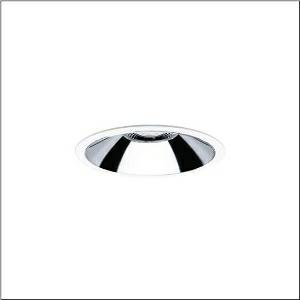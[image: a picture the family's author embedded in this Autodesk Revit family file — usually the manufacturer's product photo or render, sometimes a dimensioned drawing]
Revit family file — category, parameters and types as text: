
# Revit family: lunis_21_xl_51db15mf3d
name_source: partatom
category: Lighting Fixtures
units: mm (PartAtom-declared; Revit-internal decimal feet)

## family parameters
Cut with Voids When Loaded = No
Host = Face
Light Source = No
Part Type = Normal
Room Calculation Point = No
Round Connector Dimension = Use Diameter
Shared = No

## types (1)
- --- (1 x LED, 2620 lm, 23.5 W, 3000K)
    Apparent Load = 24 VA
    CIE Flux Codes = 89 99 100 100 100
    Color Rendering = 80
    Color Temperature = 3000K
    Default Elevation = 1800 mm
    Description = Lunis 21,  XL, downlight, of PC, light emission: direct distribution, LED rated luminous flux: 2.180lm, light colour: 830, control gear: ECG, with terminal, 3-pole, mains connection: 220..240V, AC, housing, round, of diecast aluminium, traffic white (RAL 9016), diameter: 213mm, protection rating (complete): IP20, protection rating (on room side): IP54, insulation class (complete): insulation class II (safety insulation), certification: CE, impact resistance: IK02, packaging unit: 1 piece
    Height = 0 mm  [stored 0 ft]
    Lamp = 1 x LED
    Lamp Light Flux = 2620 lm
    Lamp Power = 23.5 W
    Lamp count = 1
    Length = 213 mm
    Luminous efficacy = 111 lm/W
    Manufacturer = Siteco
    ModVariant = No
    Model = 51DB15MF3D
    Mounting Place = Ceiling
    Mounting Type = Recessed
    Number of Poles = 1
    OnlyDefault = Yes
    Power Factor = 1
    Product Name = Lunis 21 XL
    Product group = downlight
    ProductGroupID = 400
    Protection Class = Protection class II
    Protection Degree = IP 20
    RLX_Detail_Level = 1
    RLX_Emergency_Light_Flux = 0 lm
    RLX_Emergency_Type = 0
    RLX_Emergency_Type_DB = No
    RlxData = <blob elided: 27589 chars, md5=e15b8f25>
    Socket = socket
    Standby Power = 0 W
    System Light Flux = 2620 lm
    System Power = 24 W
    Type Comments = factory setting: luminous flux: 100 % | (ON | ON)
    Type Image = l_1287385.jpg
    URL = http://relux.com
    VarID = @adj_150920
    Voltage = 0 V
    Weight = 0.00 kg
    Width = 0 mm  [stored 0 ft]

note: [stored X ft] marks values corroborated as IEEE doubles in the binary element streams (Revit-internal decimal feet)

## geometry (parser evidence)
native form markers: Blend x4, Sweep x11
no freeform markers — native parametric forms only
